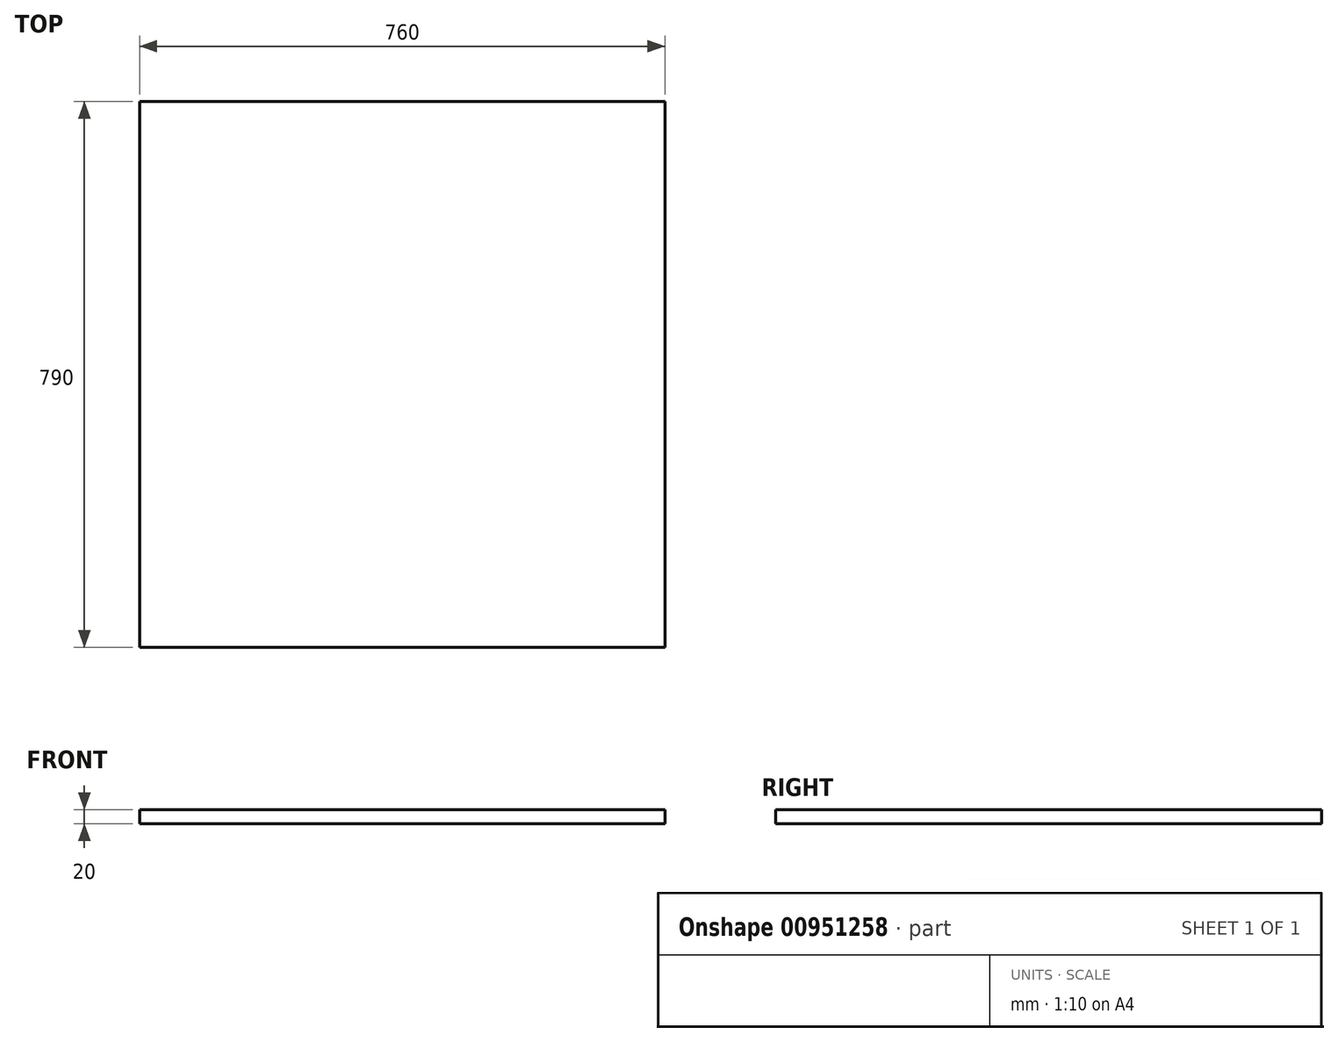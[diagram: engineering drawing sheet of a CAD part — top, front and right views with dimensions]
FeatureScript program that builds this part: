
annotation { "Feature Type Name" : "Feature", "Feature Type Description" : "" }
export const myFeature = defineFeature(function(context is Context, id is Id, definition is map)
    precondition{}
    {
        {
            var Q0;
            Q0=qCreatedBy(makeId("Top.planeOp"),FACE);
            var sketch = newSketch(context, id + "F0", { "sketchPlane" : qUnion([Q0])});
            skLineSegment(sketch, "E0.bottom", {"start": v(-60.22, 751.97) * mm, "end": v(699.78, 751.97) * mm});
            skLineSegment(sketch, "E0.top", {"start": v(-60.22, -38.03) * mm, "end": v(699.78, -38.03) * mm});
            skLineSegment(sketch, "E0.left", {"start": v(-60.22, 751.97) * mm, "end": v(-60.22, -38.03) * mm});
            skLineSegment(sketch, "E0.right", {"start": v(699.78, 751.97) * mm, "end": v(699.78, -38.03) * mm});
            skSolve(sketch);
        }
        {
            var Q0;
            Q0=qSketchRegion(id+"F0",true);
            extrude(context, id + "F1", {"entities" : qUnion([Q0]), "depth" : 20 * mm, "offsetDistance" : 25 * mm});
        }
    });
